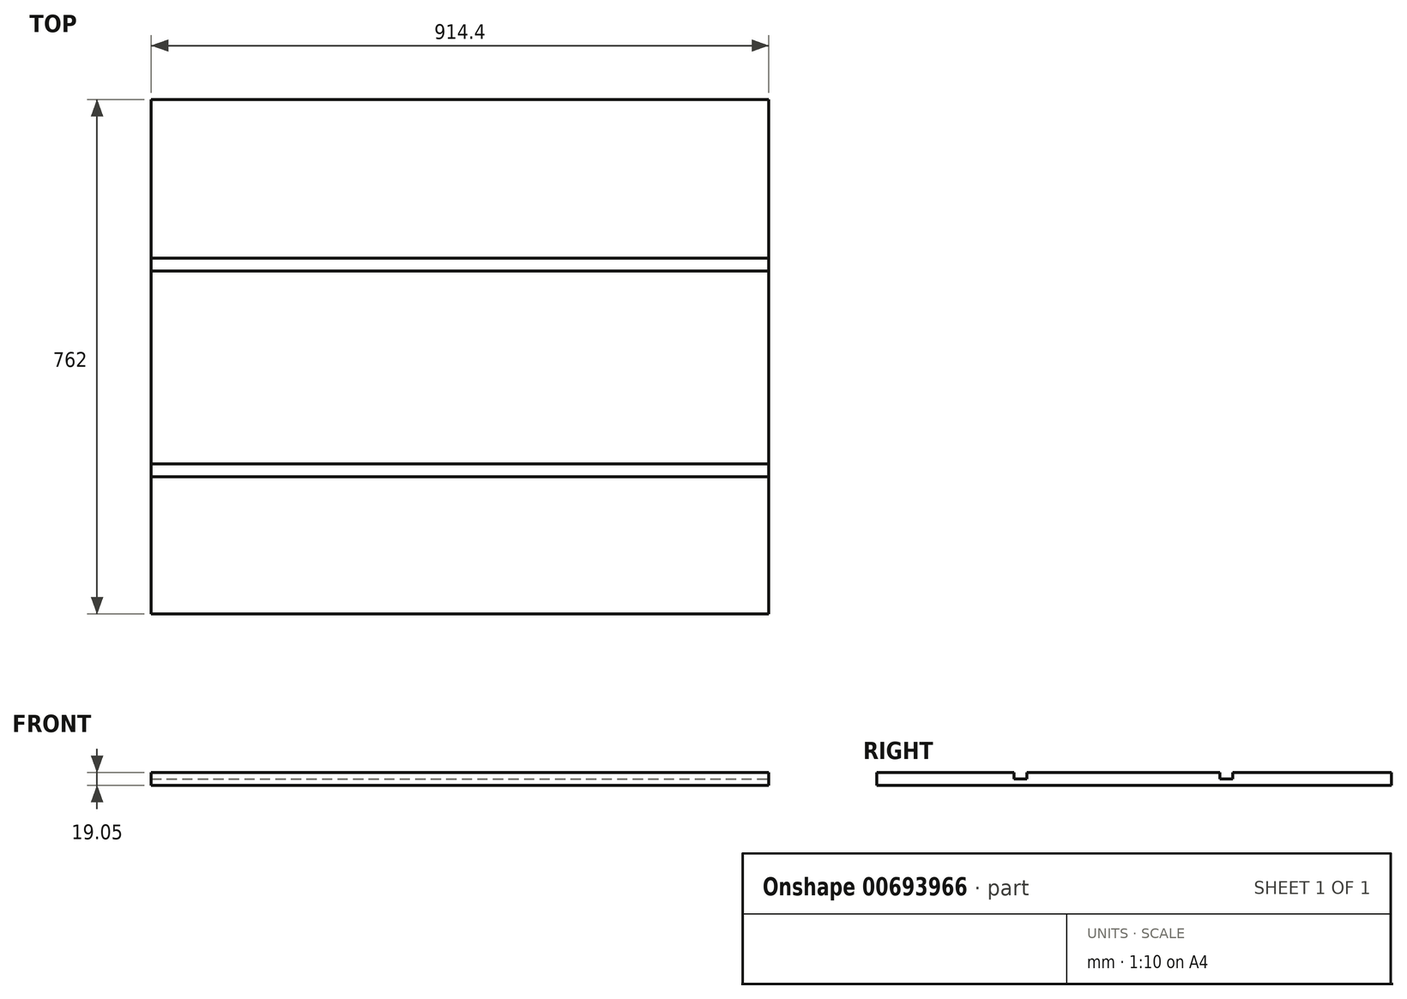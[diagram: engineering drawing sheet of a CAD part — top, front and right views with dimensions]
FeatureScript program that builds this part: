
annotation { "Feature Type Name" : "Feature", "Feature Type Description" : "" }
export const myFeature = defineFeature(function(context is Context, id is Id, definition is map)
    precondition{}
    {
        {
            var Q0;
            Q0=qCreatedBy(makeId("Right.planeOp"),FACE);
            var sketch = newSketch(context, id + "F0", { "sketchPlane" : qUnion([Q0])});
            skLineSegment(sketch, "E0.bottom", {"start": v(0, 0) * mm, "end": v(762, 0) * mm});
            skLineSegment(sketch, "E0.top", {"start": v(0, 19.05) * mm, "end": v(762, 19.05) * mm});
            skLineSegment(sketch, "E0.left", {"start": v(0, 0) * mm, "end": v(0, 19.05) * mm});
            skLineSegment(sketch, "E0.right", {"start": v(762, 0) * mm, "end": v(762, 19.05) * mm});
            skSolve(sketch);
        }
        {
            var Q0;
            Q0 = qSketchRegion(id + "F0", true);
            extrude(context, id + "F1", {"entities" : qUnion([Q0]), "oppositeDirection" : true, "depth" : 914.4 * mm, "offsetDistance" : 25.4 * mm});
        }
        {
            var Q0;
            Q0=makeQuery(id+"F1.opExtrude","CAP_FACE",FACE,{"disambiguationData":[OSD([sQuery(id+"F0.wireOp",EDGE,"E0.bottom"),sQuery(id+"F0.wireOp",EDGE,"E0.top"),sQuery(id+"F0.wireOp",EDGE,"E0.left"),sQuery(id+"F0.wireOp",EDGE,"E0.right")])],"isStart":true});
            var sketch = newSketch(context, id + "F2", { "sketchPlane" : qUnion([Q0])});
            skLineSegment(sketch, "E1.bottom", {"start": v(203.2, 19.05) * mm, "end": v(222.25, 19.05) * mm});
            skLineSegment(sketch, "E1.top", {"start": v(203.2, 9.53) * mm, "end": v(222.25, 9.53) * mm});
            skLineSegment(sketch, "E1.left", {"start": v(203.2, 19.05) * mm, "end": v(203.2, 9.53) * mm});
            skLineSegment(sketch, "E1.right", {"start": v(222.25, 19.05) * mm, "end": v(222.25, 9.53) * mm});
            skLineSegment(sketch, "E2.1.0.0", {"start": v(508, 19.05) * mm, "end": v(527.05, 19.05) * mm});
            skLineSegment(sketch, "E2.1.0.1", {"start": v(508, 9.53) * mm, "end": v(527.05, 9.53) * mm});
            skLineSegment(sketch, "E2.1.0.2", {"start": v(508, 19.05) * mm, "end": v(508, 9.53) * mm});
            skLineSegment(sketch, "E2.1.0.3", {"start": v(527.05, 19.05) * mm, "end": v(527.05, 9.53) * mm});
            skLineSegment(sketch, "E2.direction1", {"start": v(203.2, 19.05) * mm, "end": v(508, 19.05) * mm, "construction": true});
            skSolve(sketch);
        }
        {
            var Q0;
            Q0=makeQuery(id+"F2.imprint","IMPRINT",FACE,{"disambiguationData":[TD([[makeQuery(id+"F2.imprint","IMPRINT",EDGE,{"derivedFrom":sQuery(id+"F2.wireOp",EDGE,"E1.bottom")}),-1.0]])]});
            var Q1;
            Q1=makeQuery(id+"F2.imprint","IMPRINT",FACE,{"disambiguationData":[TD([[makeQuery(id+"F2.imprint","IMPRINT",EDGE,{"derivedFrom":sQuery(id+"F2.wireOp",EDGE,"E2.1.0.0")}),-1.0]])]});
            extrude(context, id + "F3", {"entities" : qUnion([Q0, Q1]), "operationType" : NewBodyOperationType.REMOVE, "endBound" : BoundingType.THROUGH_ALL, "oppositeDirection" : true, "depth" : 25.4 * mm, "offsetDistance" : 25.4 * mm});
        }
        {
            var Q0;
            Q0=makeQuery(id+"F1.opExtrude","SWEPT_FACE",FACE,{"disambiguationData":[OSD([sQuery(id+"F0.wireOp",EDGE,"E0.bottom")])]});
            var sketch = newSketch(context, id + "F4", { "sketchPlane" : qUnion([Q0])});
            skLineSegment(sketch, "E3.bottom", {"start": v(-914.4, -12.7) * mm, "end": v(-876.3, -12.7) * mm});
            skLineSegment(sketch, "E3.top", {"start": v(-914.4, -50.8) * mm, "end": v(-876.3, -50.8) * mm});
            skLineSegment(sketch, "E3.left", {"start": v(-914.4, -12.7) * mm, "end": v(-914.4, -50.8) * mm});
            skLineSegment(sketch, "E3.right", {"start": v(-876.3, -12.7) * mm, "end": v(-876.3, -50.8) * mm});
            skSolve(sketch);
        }
        {
            var Q0;
            Q0 = qSketchRegion(id + "F4", true);
            extrude(context, id + "F5", {"entities" : qUnion([Q0]), "depth" : 711.2 * mm, "offsetDistance" : 25.4 * mm});
        }
        {
            var Q0;
            Q0=makeQuery(id+"F5.opExtrude","SWEPT_BODY",BODY,{"disambiguationData":[OSD([sQuery(id+"F4.wireOp",EDGE,"E3.bottom"),sQuery(id+"F4.wireOp",EDGE,"E3.top"),sQuery(id+"F4.wireOp",EDGE,"E3.left"),sQuery(id+"F4.wireOp",EDGE,"E3.right")])]});
            deleteBodies(context, id + "F6", {"entities" : qUnion([Q0])});
        }
    });
